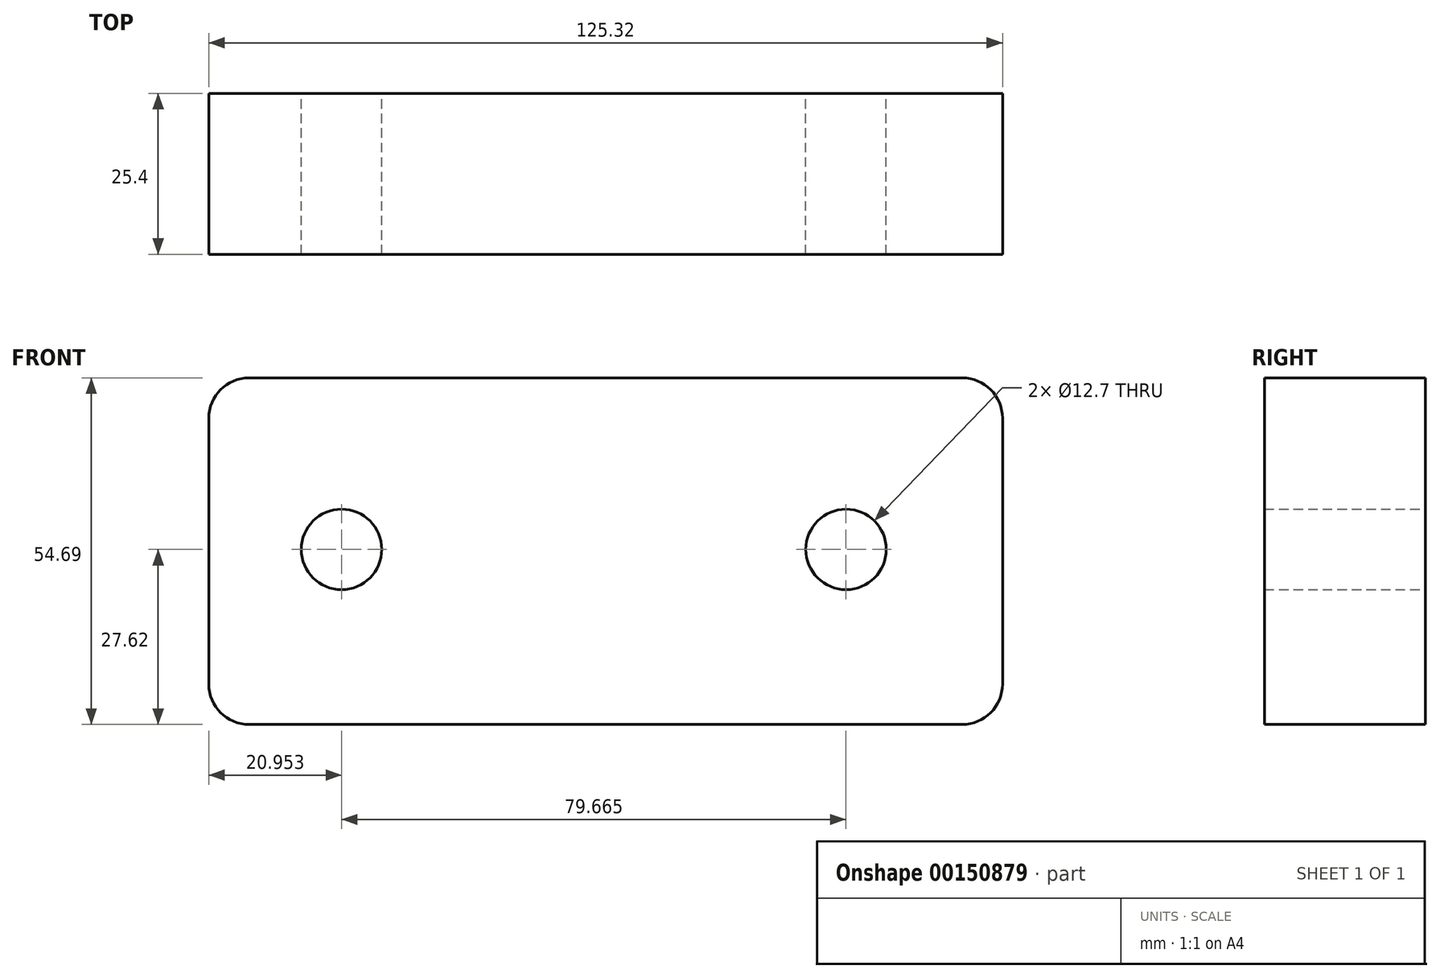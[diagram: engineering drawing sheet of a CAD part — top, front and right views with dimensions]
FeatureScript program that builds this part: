
annotation { "Feature Type Name" : "Feature", "Feature Type Description" : "" }
export const myFeature = defineFeature(function(context is Context, id is Id, definition is map)
    precondition{}
    {
        {
            var Q0;
            Q0=qCreatedBy(makeId("Front.planeOp"),FACE);
            var sketch = newSketch(context, id + "F0", { "sketchPlane" : qUnion([Q0])});
            skLineSegment(sketch, "E0", {"start": v(-60.78, 20.72) * mm, "end": v(-60.78, -21.27) * mm});
            skLineSegment(sketch, "E1", {"start": v(-54.43, -27.62) * mm, "end": v(58.2, -27.62) * mm});
            skLineSegment(sketch, "E2", {"start": v(64.54, -21.27) * mm, "end": v(64.54, 20.72) * mm});
            skLineSegment(sketch, "E3", {"start": v(58.2, 27.07) * mm, "end": v(-54.43, 27.07) * mm});
            skCircle(sketch, "E4", {"center": v(39.84, 0) * mm, "radius": 6.35 * mm});
            skPoint(sketch, "E5.visualSharp", {"position": v(64.54, 27.07) * mm});
            skArc(sketch, "E5.filletArc", {"start": v(64.54, 20.72) * mm, "mid": v(62.68, 25.2) * mm, "end": v(58.2, 27.07) * mm});
            skPoint(sketch, "E6.visualSharp", {"position": v(64.54, -27.62) * mm});
            skArc(sketch, "E6.filletArc", {"start": v(58.2, -27.62) * mm, "mid": v(62.68, -25.76) * mm, "end": v(64.54, -21.27) * mm});
            skPoint(sketch, "E7.visualSharp", {"position": v(-60.78, 27.07) * mm});
            skArc(sketch, "E7.filletArc", {"start": v(-54.43, 27.07) * mm, "mid": v(-58.92, 25.2) * mm, "end": v(-60.78, 20.72) * mm});
            skPoint(sketch, "E8.visualSharp", {"position": v(-60.78, -27.62) * mm});
            skArc(sketch, "E8.filletArc", {"start": v(-60.78, -21.27) * mm, "mid": v(-58.92, -25.76) * mm, "end": v(-54.43, -27.62) * mm});
            skCircle(sketch, "E9", {"center": v(-39.83, 0) * mm, "radius": 6.35 * mm});
            skSolve(sketch);
        }
        {
            var Q0;
            Q0=makeQuery(id+"F0.imprint","IMPRINT",FACE,{"disambiguationData":[TD([[makeQuery(id+"F0.imprint","IMPRINT",EDGE,{"derivedFrom":sQuery(id+"F0.wireOp",EDGE,"E0")}),1.0]])]});
            extrude(context, id + "F1", {"entities" : qUnion([Q0]), "depth" : 25.4 * mm});
        }
    });
